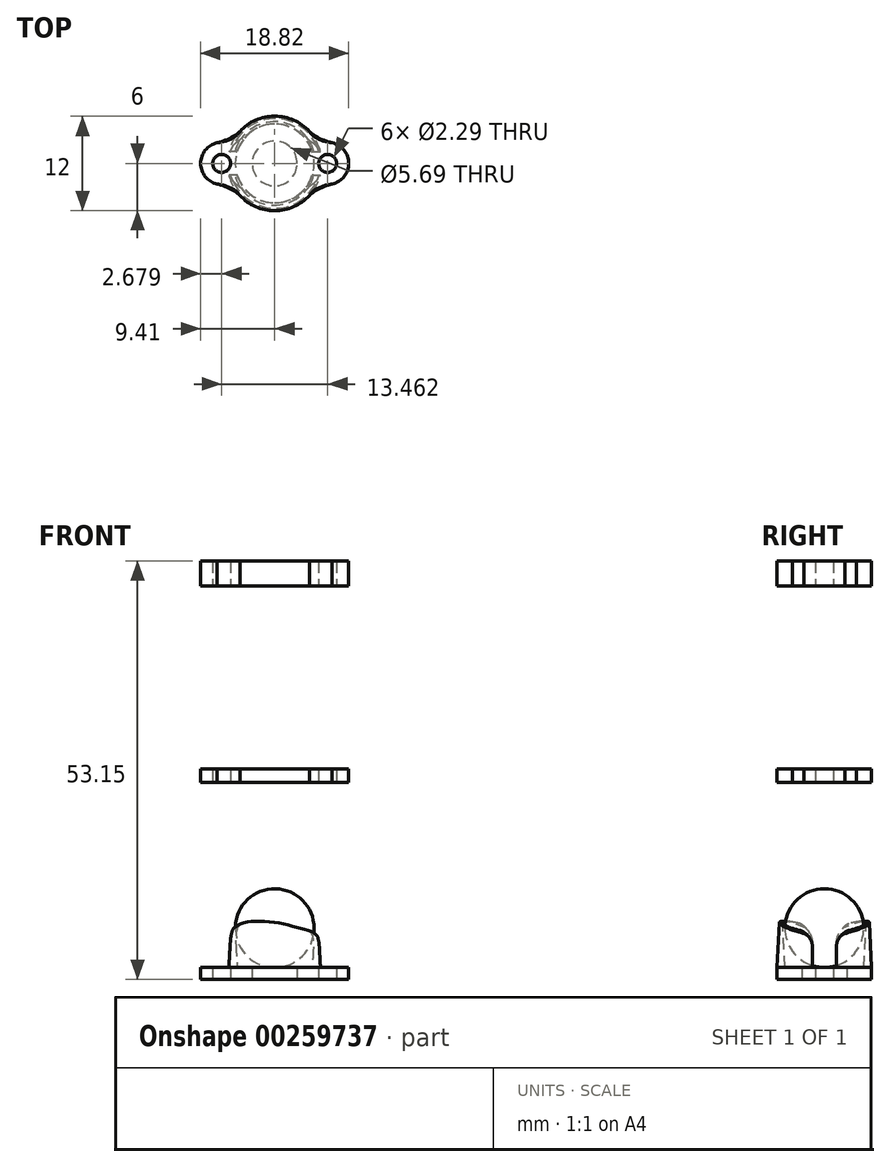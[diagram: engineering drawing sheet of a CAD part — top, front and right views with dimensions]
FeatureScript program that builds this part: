
annotation { "Feature Type Name" : "Feature", "Feature Type Description" : "" }
export const myFeature = defineFeature(function(context is Context, id is Id, definition is map)
    precondition{}
    {
        {
            var Q0;
            Q0=qCreatedBy(makeId("Top.planeOp"),FACE);
            var sketch = newSketch(context, id + "F0", { "sketchPlane" : qUnion([Q0])});
            skCircle(sketch, "E0", {"center": v(-6.73, 0) * mm, "radius": 1.14 * mm});
            skCircle(sketch, "E1", {"center": v(6.73, 0) * mm, "radius": 1.14 * mm});
            skArc(sketch, "E2", {"start": v(-4.43, -4.06) * mm, "mid": v(0, -6) * mm, "end": v(4.43, -4.06) * mm});
            skArc(sketch, "E3", {"start": v(-7.3, 2.62) * mm, "mid": v(-9.4, 0) * mm, "end": v(-7.3, -2.62) * mm});
            skArc(sketch, "E4", {"start": v(7.3, -2.62) * mm, "mid": v(9.4, 0) * mm, "end": v(7.3, 2.62) * mm});
            skCircle(sketch, "E5", {"center": v(0, 0) * mm, "radius": 2.85 * mm});
            skPoint(sketch, "E6", {"position": v(-5.51, 2.38) * mm});
            skArc(sketch, "E7.trimOffspring", {"start": v(4.43, 4.06) * mm, "mid": v(0, 6) * mm, "end": v(-4.43, 4.06) * mm});
            skFitSpline(sketch, "E8", {"points": [v(-7.3, 2.62) * mm, v(-4.43, 4.06) * mm], "startDerivative": vector(3.28, 0.71) * mm, "endDerivative": vector(1.57, 1.72) * mm});
            skFitSpline(sketch, "E9.MirrorCS", {"points": [v(-7.3, -2.62) * mm, v(-4.43, -4.06) * mm], "startDerivative": vector(3.28, -0.71) * mm, "endDerivative": vector(1.57, -1.72) * mm});
            skFitSpline(sketch, "E10.MirrorCS", {"points": [v(7.3, 2.62) * mm, v(4.43, 4.06) * mm], "startDerivative": vector(-3.28, 0.71) * mm, "endDerivative": vector(-1.57, 1.72) * mm});
            skFitSpline(sketch, "E11.MirrorCS", {"points": [v(7.3, -2.62) * mm, v(4.43, -4.06) * mm], "startDerivative": vector(-3.28, -0.71) * mm, "endDerivative": vector(-1.57, -1.72) * mm});
            skSolve(sketch);
        }
        {
            var Q0;
            Q0 = qSketchRegion(id + "F0", true);
            extrude(context, id + "F1", {"entities" : qUnion([Q0]), "depth" : 1.5 * mm});
        }
        {
            var Q0;
            Q0=makeQuery(id+"F1.opExtrude","CAP_FACE",FACE,{"disambiguationData":[OSD([sQuery(id+"F0.wireOp",EDGE,"E0"),sQuery(id+"F0.wireOp",EDGE,"E1"),sQuery(id+"F0.wireOp",EDGE,"E2"),sQuery(id+"F0.wireOp",EDGE,"E3"),sQuery(id+"F0.wireOp",EDGE,"E4"),sQuery(id+"F0.wireOp",EDGE,"E5"),sQuery(id+"F0.wireOp",EDGE,"E7.trimOffspring"),sQuery(id+"F0.wireOp",EDGE,"E8"),sQuery(id+"F0.wireOp",EDGE,"E9.MirrorCS"),sQuery(id+"F0.wireOp",EDGE,"E10.MirrorCS"),sQuery(id+"F0.wireOp",EDGE,"E11.MirrorCS")])],"isStart":false});
            var sketch = newSketch(context, id + "F2", { "sketchPlane" : qUnion([Q0])});
            skCircle(sketch, "E12", {"center": v(0, 0) * mm, "radius": 6 * mm});
            skCircle(sketch, "E13.0", {"center": v(0, 0) * mm, "radius": 5 * mm});
            skSolve(sketch);
        }
        {
            var Q0;
            Q0=makeQuery(id+"F2.imprint","IMPRINT",FACE,{"disambiguationData":[TD([[makeQuery(id+"F2.imprint","IMPRINT",EDGE,{"derivedFrom":sQuery(id+"F2.wireOp",EDGE,"E13.0")}),-1.0]])]});
            extrude(context, id + "F3", {"entities" : qUnion([Q0]), "operationType" : NewBodyOperationType.ADD, "depth" : 5.9 * mm, "hasDraft" : true, "draftAngle" : 3 * degree, "draftPullDirection" : true});
        }
        {
            var Q0;
            Q0=qCreatedBy(makeId("Front.planeOp"),FACE);
            var sketch = newSketch(context, id + "F4", { "sketchPlane" : qUnion([Q0])});
            skFitSpline(sketch, "E14", {"points": [v(-5.95, 1.5) * mm, v(-5.77, 4.78) * mm, v(-5.4, 6.25) * mm, v(-4.4, 7.04) * mm, v(-2.83, 7.35) * mm, v(-0.78, 7.32) * mm, v(0.86, 7.09) * mm, v(3.12, 6.53) * mm, v(3.88, 6.33) * mm, v(4.8, 6.01) * mm, v(5.18, 5.77) * mm, v(5.46, 5.4) * mm, v(5.74, 4.49) * mm, v(5.95, 1.5) * mm], "startDerivative": vector(0, 30.3) * mm, "endDerivative": vector(1.07, -30.08) * mm});
            skLineSegment(sketch, "E15", {"start": v(-5.95, 1.5) * mm, "end": v(5.95, 1.5) * mm});
            skLineSegment(sketch, "E16", {"start": v(-5.95, 1.5) * mm, "end": v(-9.53, 1.5) * mm});
            skLineSegment(sketch, "E17", {"start": v(-9.53, 1.5) * mm, "end": v(-9.53, 0) * mm});
            skLineSegment(sketch, "E18", {"start": v(-9.53, 0) * mm, "end": v(9.53, 0) * mm});
            skLineSegment(sketch, "E19", {"start": v(9.53, 0) * mm, "end": v(9.53, 1.5) * mm});
            skLineSegment(sketch, "E20", {"start": v(9.53, 1.5) * mm, "end": v(5.95, 1.5) * mm});
            skSolve(sketch);
        }
        {
            var Q0;
            Q0 = qSketchRegion(id + "F4", true);
            extrude(context, id + "F5", {"entities" : qUnion([Q0]), "operationType" : NewBodyOperationType.INTERSECT, "endBound" : BoundingType.SYMMETRIC, "depth" : 25 * mm});
        }
        {
            var Q0;
            Q0=qCreatedBy(makeId("Right.planeOp"),FACE);
            var Q1;
            {var subQ0=sQuery(id+"F2.wireOp",EDGE,"E12");var subQ1=sQuery(id+"F0.wireOp",EDGE,"E0");Q1=makeQuery(id+"F3.opExtrude","CAP_VERTEX",VERTEX,{"disambiguationData":[OSD([subQ1,subQ0]),TDD([makeQuery(id+"F2.imprint","INTERSECT",VERTEX,{"disambiguationData":[OD(0.0)],"derivedFrom":[makeQuery(id+"F1.opExtrude","CAP_EDGE",EDGE,{"disambiguationData":[OSD([subQ1])],"isStart":false}),subQ0]})])],"isStart":true});}
            cPlane(context, id + "F6", {"entities" : qUnion([Q0, Q1]), "cplaneType" : CPlaneType.PLANE_POINT, "offset" : 25 * mm, "width" : 150 * mm, "height" : 150 * mm});
        }
        {
            var Q0;
            Q0=qCreatedBy(id+"F6.planeOp",FACE);
            var sketch = newSketch(context, id + "F7", { "sketchPlane" : qUnion([Q0])});
            skLineSegment(sketch, "E21.bottom", {"start": v(1.5, 1.5) * mm, "end": v(-1.5, 1.5) * mm});
            skLineSegment(sketch, "E21.left", {"start": v(1.5, 1.5) * mm, "end": v(1.5, 4.42) * mm});
            skLineSegment(sketch, "E21.right", {"start": v(-1.5, 1.5) * mm, "end": v(-1.5, 4.42) * mm});
            skLineSegment(sketch, "E22", {"start": v(-4.5, 7.42) * mm, "end": v(-6.48, 7.42) * mm});
            skLineSegment(sketch, "E23", {"start": v(-6.48, 7.42) * mm, "end": v(-6.48, 8.72) * mm});
            skLineSegment(sketch, "E24", {"start": v(6.48, 8.72) * mm, "end": v(6.48, 7.42) * mm});
            skLineSegment(sketch, "E25", {"start": v(6.48, 7.42) * mm, "end": v(4.5, 7.42) * mm});
            skPoint(sketch, "E26.newPointB", {"position": v(-4.16, 7.42) * mm});
            skArc(sketch, "E26.filletArc", {"start": v(-1.5, 4.42) * mm, "mid": v(-2.38, 6.55) * mm, "end": v(-4.5, 7.42) * mm});
            skPoint(sketch, "E27.newPointA", {"position": v(-1.16, 7.42) * mm});
            skArc(sketch, "E27.filletArc", {"start": v(4.5, 7.42) * mm, "mid": v(2.38, 6.55) * mm, "end": v(1.5, 4.42) * mm});
            skLineSegment(sketch, "E28", {"start": v(6.48, 8.72) * mm, "end": v(-6.48, 8.72) * mm});
            skSolve(sketch);
        }
        {
            var Q0;
            Q0=makeQuery(id+"F7.imprint","IMPRINT",FACE,{"disambiguationData":[TD([[makeQuery(id+"F7.imprint","IMPRINT",EDGE,{"derivedFrom":sQuery(id+"F7.wireOp",EDGE,"E21.bottom")}),-1.0]])]});
            extrude(context, id + "F8", {"entities" : qUnion([Q0]), "operationType" : NewBodyOperationType.REMOVE, "depth" : 5 * mm});
        }
        {
            var Q0;
            Q0=qCreatedBy(makeId("Right.planeOp"),FACE);
            var Q1;
            {var subQ0=sQuery(id+"F2.wireOp",EDGE,"E12");var subQ1=sQuery(id+"F0.wireOp",EDGE,"E1");Q1=makeQuery(id+"F3.opExtrude","CAP_VERTEX",VERTEX,{"disambiguationData":[OSD([subQ1,subQ0]),TDD([makeQuery(id+"F2.imprint","INTERSECT",VERTEX,{"disambiguationData":[OD(1.0)],"derivedFrom":[makeQuery(id+"F1.opExtrude","CAP_EDGE",EDGE,{"disambiguationData":[OSD([subQ1])],"isStart":false}),subQ0]})])],"isStart":true});}
            cPlane(context, id + "F9", {"entities" : qUnion([Q0, Q1]), "cplaneType" : CPlaneType.PLANE_POINT, "offset" : 25 * mm, "width" : 150 * mm, "height" : 150 * mm});
        }
        {
            var Q0;
            Q0=qCreatedBy(id+"F9.planeOp",FACE);
            var sketch = newSketch(context, id + "F10", { "sketchPlane" : qUnion([Q0])});
            skLineSegment(sketch, "E29", {"start": v(-1.5, 1.5) * mm, "end": v(-1.5, 3.98) * mm});
            skLineSegment(sketch, "E30.bottom", {"start": v(-1.5, 1.5) * mm, "end": v(0, 1.5) * mm});
            skLineSegment(sketch, "E30.left", {"start": v(-1.5, 1.5) * mm, "end": v(-1.5, 1.5) * mm});
            skLineSegment(sketch, "E30.right", {"start": v(0, 1.5) * mm, "end": v(0, 1.5) * mm});
            skArc(sketch, "E31", {"start": v(-1.5, 3.98) * mm, "mid": v(-1.97, 5.4) * mm, "end": v(-3.18, 6.25) * mm});
            skLineSegment(sketch, "E32", {"start": v(-3.18, 6.25) * mm, "end": v(-3.18, 6.91) * mm});
            skLineSegment(sketch, "E33", {"start": v(-3.18, 6.91) * mm, "end": v(0, 6.91) * mm});
            skLineSegment(sketch, "E34.MirrorCS", {"start": v(3.18, 6.91) * mm, "end": v(0, 6.91) * mm});
            skLineSegment(sketch, "E35.MirrorCS", {"start": v(3.18, 6.25) * mm, "end": v(3.18, 6.91) * mm});
            skArc(sketch, "E36.MirrorCS", {"start": v(1.5, 3.98) * mm, "mid": v(1.97, 5.4) * mm, "end": v(3.18, 6.25) * mm});
            skLineSegment(sketch, "E37.MirrorCS", {"start": v(1.5, 1.5) * mm, "end": v(1.5, 3.98) * mm});
            skLineSegment(sketch, "E38.MirrorCS", {"start": v(1.5, 1.5) * mm, "end": v(0, 1.5) * mm});
            skSolve(sketch);
        }
        {
            var Q0;
            Q0 = qSketchRegion(id + "F10", true);
            extrude(context, id + "F11", {"entities" : qUnion([Q0]), "operationType" : NewBodyOperationType.REMOVE, "oppositeDirection" : true, "depth" : 3 * mm});
        }
        {
            var Q0;
            {var subQ0=sQuery(id+"F0.wireOp",EDGE,"E7.trimOffspring");var subQ2=sQuery(id+"F0.wireOp",EDGE,"E0");var subQ3=sQuery(id+"F0.wireOp",EDGE,"E3");var subQ4=sQuery(id+"F0.wireOp",EDGE,"E2");var subQ6=sQuery(id+"F0.wireOp",EDGE,"E8");var subQ7=sQuery(id+"F0.wireOp",EDGE,"E9.MirrorCS");var subQ11=sQuery(id+"F0.wireOp",EDGE,"E10.MirrorCS");var subQ13=sQuery(id+"F0.wireOp",EDGE,"E1");var subQ16=sQuery(id+"F0.wireOp",EDGE,"E11.MirrorCS");var subQ20=sQuery(id+"F0.wireOp",EDGE,"E5");var subQ21=sQuery(id+"F0.wireOp",EDGE,"E4");var subQ22=makeQuery(id+"F1.opExtrude","CAP_FACE",FACE,{"disambiguationData":[OSD([subQ2,subQ13,subQ4,subQ3,subQ21,subQ20,subQ0,subQ6,subQ7,subQ11,subQ16])],"isStart":false});Q0=makeQuery(id+"F11.boolean.opBoolean","MERGE",FACE,{"derivedFrom":[makeQuery(id+"F3.boolean.opBoolean","SPLIT",FACE,{"disambiguationData":[TD([makeQuery(id+"F1.opExtrude","SWEPT_FACE",FACE,{"disambiguationData":[OSD([subQ13])]})])],"derivedFrom":subQ22}),makeQuery(id+"F8.boolean.opBoolean","MERGE",FACE,{"derivedFrom":[makeQuery(id+"F3.boolean.opBoolean","SPLIT",FACE,{"disambiguationData":[TD([makeQuery(id+"F1.opExtrude","SWEPT_FACE",FACE,{"disambiguationData":[OSD([subQ20])]})])],"derivedFrom":subQ22}),makeQuery(id+"F3.boolean.opBoolean","SPLIT",FACE,{"disambiguationData":[TD([makeQuery(id+"F1.opExtrude","SWEPT_FACE",FACE,{"disambiguationData":[OSD([subQ2])]})])],"derivedFrom":subQ22}),makeQuery(id+"F8.opExtrude","SWEPT_FACE",FACE,{"disambiguationData":[OSD([sQuery(id+"F7.wireOp",EDGE,"E21.bottom")])]})]}),makeQuery(id+"F11.opExtrude","SWEPT_FACE",FACE,{"disambiguationData":[OSD([sQuery(id+"F10.wireOp",EDGE,"E30.bottom"),sQuery(id+"F10.wireOp",EDGE,"E38.MirrorCS")])]})]});}
            cPlane(context, id + "F12", {"entities" : qUnion([Q0]), "cplaneType" : CPlaneType.OFFSET, "offset" : 5 * mm, "width" : 150 * mm, "height" : 150 * mm});
        }
        {
            var Q0;
            Q0=qCreatedBy(id+"F12.planeOp",FACE);
            var sketch = newSketch(context, id + "F13", { "sketchPlane" : qUnion([Q0])});
            skArc(sketch, "E39", {"start": v(0, 5) * mm, "mid": v(-5, 0) * mm, "end": v(0, -5) * mm});
            skLineSegment(sketch, "E40", {"start": v(0, -5) * mm, "end": v(0, 5) * mm, "construction": true});
            skLineSegment(sketch, "E41", {"start": v(0, -5) * mm, "end": v(0, 5) * mm});
            skSolve(sketch);
        }
        {
            var Q0;
            Q0=makeQuery(id+"F13.imprint","IMPRINT",FACE,{"disambiguationData":[TD([[makeQuery(id+"F13.imprint","IMPRINT",EDGE,{"derivedFrom":sQuery(id+"F13.wireOp",EDGE,"E39")}),1.0]])]});
            var Q1;
            Q1=sQuery(id+"F13.wireOp",EDGE,"E40");
            revolve(context, id + "F14", {"entities" : qUnion([Q0]), "axis" : qUnion([Q1]), "revolveType" : RevolveType.FULL});
        }
        {
            var Q0;
            Q0=qCreatedBy(makeId("Top.planeOp"),FACE);
            cPlane(context, id + "F15", {"entities" : qUnion([Q0]), "cplaneType" : CPlaneType.OFFSET, "offset" : 25 * mm, "width" : 150 * mm, "height" : 150 * mm});
        }
        {
            var Q0;
            Q0=qCreatedBy(id+"F15.planeOp",FACE);
            var sketch = newSketch(context, id + "F16", { "sketchPlane" : qUnion([Q0])});
            skFitSpline(sketch, "E42.0.0", {"points": [v(4.43, 4.06) * mm, v(4.95, 3.48) * mm, v(6.2, 2.85) * mm, v(7.3, 2.62) * mm]});
            skArc(sketch, "E42.0.1", {"start": v(7.3, 2.62) * mm, "mid": v(9.4, 0) * mm, "end": v(7.3, -2.62) * mm});
            skFitSpline(sketch, "E42.0.2", {"points": [v(7.3, -2.62) * mm, v(6.2, -2.85) * mm, v(4.95, -3.48) * mm, v(4.43, -4.06) * mm]});
            skArc(sketch, "E42.0.3", {"start": v(4.43, -4.06) * mm, "mid": v(0, -6) * mm, "end": v(-4.43, -4.06) * mm});
            skFitSpline(sketch, "E42.0.4", {"points": [v(-4.43, -4.06) * mm, v(-4.95, -3.48) * mm, v(-6.2, -2.85) * mm, v(-7.3, -2.62) * mm]});
            skArc(sketch, "E42.0.5", {"start": v(-7.3, -2.62) * mm, "mid": v(-9.4, 0) * mm, "end": v(-7.3, 2.62) * mm});
            skFitSpline(sketch, "E42.0.6", {"points": [v(-7.3, 2.62) * mm, v(-6.2, 2.85) * mm, v(-4.95, 3.48) * mm, v(-4.43, 4.06) * mm]});
            skArc(sketch, "E42.0.7", {"start": v(-4.43, 4.06) * mm, "mid": v(0, 6) * mm, "end": v(4.43, 4.06) * mm});
            skCircle(sketch, "E43.0", {"center": v(-6.73, 0) * mm, "radius": 1.14 * mm});
            skCircle(sketch, "E44.0", {"center": v(6.73, 0) * mm, "radius": 1.14 * mm});
            skSolve(sketch);
        }
        {
            var Q0;
            Q0=makeQuery(id+"F16.imprint","IMPRINT",FACE,{"disambiguationData":[TD([[makeQuery(id+"F16.imprint","IMPRINT",EDGE,{"derivedFrom":sQuery(id+"F16.wireOp",EDGE,"E42.0.0")}),-1.0]])]});
            extrude(context, id + "F17", {"entities" : qUnion([Q0]), "depth" : 1.7 * mm});
        }
        {
            var Q0;
            Q0=qCreatedBy(makeId("Top.planeOp"),FACE);
            cPlane(context, id + "F18", {"entities" : qUnion([Q0]), "cplaneType" : CPlaneType.OFFSET, "offset" : 50 * mm, "width" : 150 * mm, "height" : 150 * mm});
        }
        {
            var Q0;
            Q0=qCreatedBy(id+"F18.planeOp",FACE);
            var sketch = newSketch(context, id + "F19", { "sketchPlane" : qUnion([Q0])});
            skArc(sketch, "E45.0.0", {"start": v(4.43, 4.06) * mm, "mid": v(0, 6) * mm, "end": v(-4.43, 4.06) * mm});
            skFitSpline(sketch, "E45.0.1", {"points": [v(-4.43, 4.06) * mm, v(-4.95, 3.48) * mm, v(-6.2, 2.85) * mm, v(-7.3, 2.62) * mm]});
            skArc(sketch, "E45.0.2", {"start": v(-7.3, 2.62) * mm, "mid": v(-9.4, 0) * mm, "end": v(-7.3, -2.62) * mm});
            skFitSpline(sketch, "E45.0.3", {"points": [v(-7.3, -2.62) * mm, v(-6.2, -2.85) * mm, v(-4.95, -3.48) * mm, v(-4.43, -4.06) * mm]});
            skArc(sketch, "E45.0.4", {"start": v(-4.43, -4.06) * mm, "mid": v(0, -6) * mm, "end": v(4.43, -4.06) * mm});
            skFitSpline(sketch, "E45.0.5", {"points": [v(4.43, -4.06) * mm, v(4.95, -3.48) * mm, v(6.2, -2.85) * mm, v(7.3, -2.62) * mm]});
            skArc(sketch, "E45.0.6", {"start": v(7.3, -2.62) * mm, "mid": v(9.4, 0) * mm, "end": v(7.3, 2.62) * mm});
            skFitSpline(sketch, "E45.0.7", {"points": [v(7.3, 2.62) * mm, v(6.2, 2.85) * mm, v(4.95, 3.48) * mm, v(4.43, 4.06) * mm]});
            skCircle(sketch, "E46.0", {"center": v(-6.73, 0) * mm, "radius": 1.14 * mm});
            skCircle(sketch, "E47.0", {"center": v(6.73, 0) * mm, "radius": 1.14 * mm});
            skSolve(sketch);
        }
        {
            var Q0;
            Q0=makeQuery(id+"F19.imprint","IMPRINT",FACE,{"disambiguationData":[TD([[makeQuery(id+"F19.imprint","IMPRINT",EDGE,{"derivedFrom":sQuery(id+"F19.wireOp",EDGE,"E45.0.0")}),1.0]])]});
            extrude(context, id + "F20", {"entities" : qUnion([Q0]), "depth" : 3.15 * mm});
        }
    });
